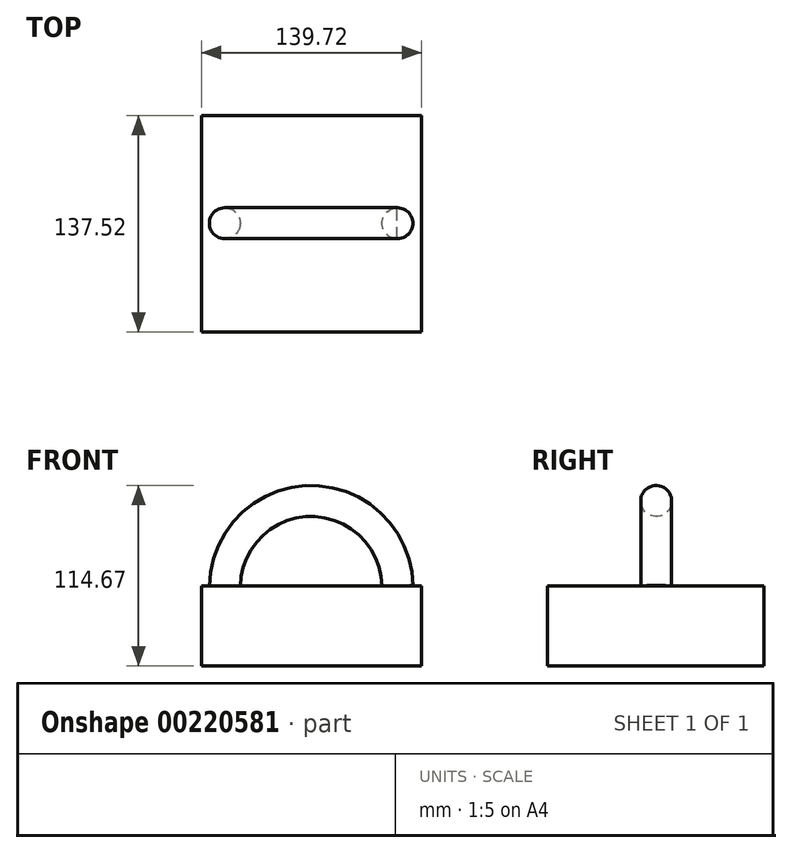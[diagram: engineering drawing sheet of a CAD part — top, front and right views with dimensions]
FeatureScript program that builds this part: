
annotation { "Feature Type Name" : "Feature", "Feature Type Description" : "" }
export const myFeature = defineFeature(function(context is Context, id is Id, definition is map)
    precondition{}
    {
        {
            var Q0;
            Q0=qCreatedBy(makeId("Top.planeOp"),FACE);
            var sketch = newSketch(context, id + "F0", { "sketchPlane" : qUnion([Q0])});
            skLineSegment(sketch, "E0.bottom", {"start": v(69.86, -68.76) * mm, "end": v(-69.86, -68.76) * mm});
            skLineSegment(sketch, "E0.top", {"start": v(69.86, 68.76) * mm, "end": v(-69.86, 68.76) * mm});
            skLineSegment(sketch, "E0.left", {"start": v(69.86, -68.76) * mm, "end": v(69.86, 68.76) * mm});
            skLineSegment(sketch, "E0.right", {"start": v(-69.86, -68.76) * mm, "end": v(-69.86, 68.76) * mm});
            skPoint(sketch, "E0.middle", {"position": v(0, 0) * mm});
            skLineSegment(sketch, "E1", {"start": v(0, 68.76) * mm, "end": v(0, -68.76) * mm});
            skSolve(sketch);
        }
        {
            var Q0;
            {var subQ0=sQuery(id+"F0.wireOp",EDGE,"E0.right");Q0=makeQuery(id+"F0.imprint","IMPRINT",FACE,{"disambiguationData":[TD([[makeQuery(id+"F0.imprint","IMPRINT",EDGE,{"derivedFrom":subQ0}),-1.0]])]});}
            var Q1;
            {var subQ0=sQuery(id+"F0.wireOp",EDGE,"E0.left");Q1=makeQuery(id+"F0.imprint","IMPRINT",FACE,{"disambiguationData":[TD([[makeQuery(id+"F0.imprint","IMPRINT",EDGE,{"derivedFrom":subQ0}),1.0]])]});}
            extrude(context, id + "F1", {"entities" : qUnion([Q0, Q1]), "oppositeDirection" : true, "depth" : 50.8 * mm});
        }
        {
            var Q0;
            {var subQ0=sQuery(id+"F0.wireOp",EDGE,"E0.right");Q0=makeQuery(id+"F0.imprint","IMPRINT",FACE,{"disambiguationData":[TD([[makeQuery(id+"F0.imprint","IMPRINT",EDGE,{"derivedFrom":subQ0}),-1.0]])]});}
            var sketch = newSketch(context, id + "F2", { "sketchPlane" : qUnion([Q0])});
            skPoint(sketch, "E2", {"position": v(-55.03, 0) * mm});
            skCircle(sketch, "E3", {"center": v(-55.03, 0.3) * mm, "radius": 9.82 * mm});
            skSolve(sketch);
        }
        {
            var Q0;
            Q0=qCreatedBy(makeId("Front.planeOp"),FACE);
            var sketch = newSketch(context, id + "F3", { "sketchPlane" : qUnion([Q0])});
            skArc(sketch, "E4", {"start": v(54.41, 0) * mm, "mid": v(-0.2, 53.85) * mm, "end": v(-54.83, 0) * mm});
            skSolve(sketch);
        }
        {
            var Q0;
            Q0=makeQuery(id+"F2.imprint","IMPRINT",FACE,{"disambiguationData":[TD([[makeQuery(id+"F2.imprint","IMPRINT",EDGE,{"derivedFrom":sQuery(id+"F2.wireOp",EDGE,"E3")}),1.0]])]});
            var Q1;
            Q1=sQuery(id+"F3.wireOp",EDGE,"E4");
            sweep(context, id + "F4", {"operationType" : NewBodyOperationType.ADD, "profiles" : qUnion([Q0]), "path" : qUnion([Q1])});
        }
    });
